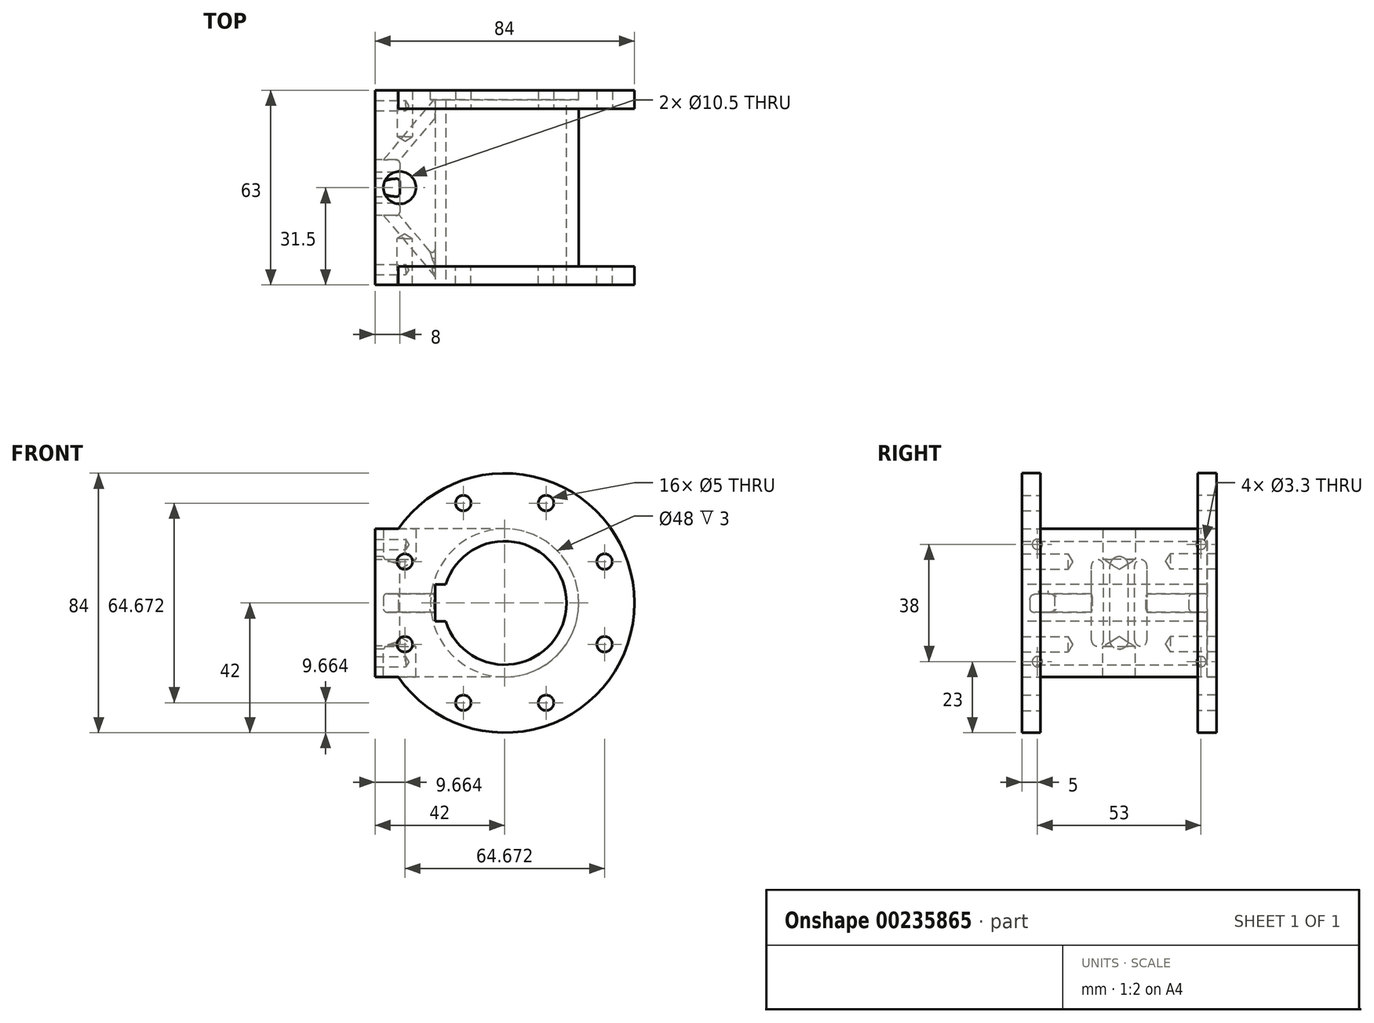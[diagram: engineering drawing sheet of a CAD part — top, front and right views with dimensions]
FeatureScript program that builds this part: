
annotation { "Feature Type Name" : "Feature", "Feature Type Description" : "" }
export const myFeature = defineFeature(function(context is Context, id is Id, definition is map)
    precondition{}
    {
        {
            var Q0;
            Q0=qCreatedBy(makeId("Front.planeOp"),FACE);
            var sketch = newSketch(context, id + "F0", { "sketchPlane" : qUnion([Q0])});
            skCircle(sketch, "E0", {"center": v(0, 0) * mm, "radius": 42 * mm});
            skCircle(sketch, "E1", {"center": v(0, 0) * mm, "radius": 35 * mm, "construction": true});
            skCircle(sketch, "E2", {"center": v(0, 0) * mm, "radius": 20 * mm});
            skCircle(sketch, "E3", {"center": v(-32.34, 13.4) * mm, "radius": 2.5 * mm});
            skCircle(sketch, "E4.1.0", {"center": v(-13.4, 32.34) * mm, "radius": 2.5 * mm});
            skCircle(sketch, "E4.2.0", {"center": v(13.4, 32.34) * mm, "radius": 2.5 * mm});
            skCircle(sketch, "E4.3.0", {"center": v(32.34, 13.4) * mm, "radius": 2.5 * mm});
            skCircle(sketch, "E4.4.0", {"center": v(32.34, -13.4) * mm, "radius": 2.5 * mm});
            skCircle(sketch, "E4.5.0", {"center": v(13.4, -32.34) * mm, "radius": 2.5 * mm});
            skCircle(sketch, "E4.6.0", {"center": v(-13.4, -32.34) * mm, "radius": 2.5 * mm});
            skCircle(sketch, "E4.7.0", {"center": v(-32.34, -13.4) * mm, "radius": 2.5 * mm});
            skLineSegment(sketch, "E4.anchor1", {"start": v(0, 0) * mm, "end": v(0, 35) * mm, "construction": true});
            skLineSegment(sketch, "E4.anchor2", {"start": v(0, 0) * mm, "end": v(-24.75, 24.75) * mm, "construction": true});
            skLineSegment(sketch, "E5", {"start": v(0, 0) * mm, "end": v(-54.86, 0) * mm, "construction": true});
            skLineSegment(sketch, "E6", {"start": v(-32.34, 13.4) * mm, "end": v(0, 0) * mm, "construction": true});
            skSolve(sketch);
        }
        {
            var Q0;
            Q0 = qSketchRegion(id + "F0", true);
            extrude(context, id + "F1", {"entities" : qUnion([Q0]), "depth" : 6 * mm});
        }
        {
            var Q0;
            Q0=qCreatedBy(makeId("Front.planeOp"),FACE);
            cPlane(context, id + "F2", {"entities" : qUnion([Q0]), "cplaneType" : CPlaneType.OFFSET, "offset" : 51 * mm, "oppositeDirection" : true, "width" : 150 * mm, "height" : 150 * mm});
        }
        {
            var Q0;
            Q0=qCreatedBy(id+"F2.planeOp",FACE);
            var sketch = newSketch(context, id + "F3", { "sketchPlane" : qUnion([Q0])});
            skCircle(sketch, "E7", {"center": v(0, 0) * mm, "radius": 42 * mm});
            skCircle(sketch, "E8", {"center": v(0, 0) * mm, "radius": 35 * mm, "construction": true});
            skCircle(sketch, "E9", {"center": v(0, 0) * mm, "radius": 20 * mm});
            skCircle(sketch, "E10", {"center": v(-32.34, 13.4) * mm, "radius": 2.5 * mm});
            skCircle(sketch, "E11.1.0", {"center": v(-32.34, -13.4) * mm, "radius": 2.5 * mm});
            skCircle(sketch, "E11.2.0", {"center": v(-13.4, -32.34) * mm, "radius": 2.5 * mm});
            skCircle(sketch, "E11.3.0", {"center": v(13.4, -32.34) * mm, "radius": 2.5 * mm});
            skCircle(sketch, "E11.4.0", {"center": v(32.34, -13.4) * mm, "radius": 2.5 * mm});
            skCircle(sketch, "E11.5.0", {"center": v(32.34, 13.4) * mm, "radius": 2.5 * mm});
            skCircle(sketch, "E11.6.0", {"center": v(13.4, 32.34) * mm, "radius": 2.5 * mm});
            skCircle(sketch, "E11.7.0", {"center": v(-13.4, 32.34) * mm, "radius": 2.5 * mm});
            skSolve(sketch);
        }
        {
            var Q0;
            Q0 = qSketchRegion(id + "F3", true);
            extrude(context, id + "F4", {"entities" : qUnion([Q0]), "oppositeDirection" : true, "depth" : 6 * mm});
        }
        {
            var Q0;
            Q0=qCreatedBy(makeId("Front.planeOp"),FACE);
            var sketch = newSketch(context, id + "F5", { "sketchPlane" : qUnion([Q0])});
            skCircle(sketch, "E12", {"center": v(0, 0) * mm, "radius": 24 * mm});
            skLineSegment(sketch, "E13", {"start": v(0, 24) * mm, "end": v(-42, 24) * mm});
            skLineSegment(sketch, "E14.0", {"start": v(0, -24) * mm, "end": v(-42, -24) * mm});
            skLineSegment(sketch, "E15", {"start": v(-42, 24) * mm, "end": v(-42, -24) * mm});
            skArc(sketch, "E16", {"start": v(-19.08, -6) * mm, "mid": v(20, 0) * mm, "end": v(-19.08, 6) * mm});
            skLineSegment(sketch, "E17", {"start": v(-22.52, -6) * mm, "end": v(-22.52, 6) * mm});
            skLineSegment(sketch, "E18", {"start": v(-22.52, 6) * mm, "end": v(-19.08, 6) * mm});
            skLineSegment(sketch, "E19", {"start": v(-19.08, -6) * mm, "end": v(-22.52, -6) * mm});
            skSolve(sketch);
        }
        {
            var Q0;
            {var subQ0=sQuery(id+"F5.wireOp",EDGE,"E13");Q0=makeQuery(id+"F5.imprint","IMPRINT",FACE,{"disambiguationData":[TD([[makeQuery(id+"F5.imprint","IMPRINT",EDGE,{"derivedFrom":subQ0}),1.0]])]});}
            var Q1;
            Q1=makeQuery(id+"F5.imprint","IMPRINT",FACE,{"disambiguationData":[TD([[makeQuery(id+"F5.imprint","IMPRINT",EDGE,{"derivedFrom":sQuery(id+"F5.wireOp",EDGE,"E16")}),-1.0]])]});
            var Q2;
            Q2=makeQuery(id+"F4.opExtrude","CAP_FACE",FACE,{"disambiguationData":[OSD([sQuery(id+"F3.wireOp",EDGE,"E7"),sQuery(id+"F3.wireOp",EDGE,"E9"),sQuery(id+"F3.wireOp",EDGE,"E10"),sQuery(id+"F3.wireOp",EDGE,"E11.1.0"),sQuery(id+"F3.wireOp",EDGE,"E11.2.0"),sQuery(id+"F3.wireOp",EDGE,"E11.3.0"),sQuery(id+"F3.wireOp",EDGE,"E11.4.0"),sQuery(id+"F3.wireOp",EDGE,"E11.5.0"),sQuery(id+"F3.wireOp",EDGE,"E11.6.0"),sQuery(id+"F3.wireOp",EDGE,"E11.7.0")])],"isStart":false});
            extrude(context, id + "F6", {"entities" : qUnion([Q0, Q1]), "operationType" : NewBodyOperationType.ADD, "endBound" : BoundingType.UP_TO_SURFACE, "oppositeDirection" : true, "endBoundEntityFace" : qUnion([Q2]), "depth" : 25 * mm});
        }
        {
            var Q0;
            {var subQ0=sQuery(id+"F5.wireOp",EDGE,"E13");Q0=makeQuery(id+"F5.imprint","IMPRINT",FACE,{"disambiguationData":[TD([[makeQuery(id+"F5.imprint","IMPRINT",EDGE,{"derivedFrom":subQ0}),1.0]])]});}
            var Q1;
            Q1=makeQuery(id+"F5.imprint","IMPRINT",FACE,{"disambiguationData":[TD([[makeQuery(id+"F5.imprint","IMPRINT",EDGE,{"derivedFrom":sQuery(id+"F5.wireOp",EDGE,"E16")}),-1.0]])]});
            extrude(context, id + "F7", {"entities" : qUnion([Q0, Q1]), "operationType" : NewBodyOperationType.ADD, "depth" : 6 * mm});
        }
        {
            var Q0;
            Q0=makeQuery(id+"F5.imprint","IMPRINT",FACE,{"disambiguationData":[TD([[makeQuery(id+"F5.imprint","IMPRINT",EDGE,{"derivedFrom":sQuery(id+"F5.wireOp",EDGE,"E16")}),1.0]])]});
            extrude(context, id + "F8", {"entities" : qUnion([Q0]), "operationType" : NewBodyOperationType.REMOVE, "oppositeDirection" : true, "depth" : 222 * mm, "symmetric" : true});
        }
        {
            var Q0;
            Q0=qCreatedBy(makeId("Front.planeOp"),FACE);
            cPlane(context, id + "F9", {"entities" : qUnion([Q0]), "cplaneType" : CPlaneType.OFFSET, "offset" : 6 * mm, "width" : 150 * mm, "height" : 150 * mm});
        }
        {
            var Q0;
            Q0=qCreatedBy(id+"F9.planeOp",FACE);
            var sketch = newSketch(context, id + "F10", { "sketchPlane" : qUnion([Q0])});
            skCircle(sketch, "E20", {"center": v(0, 0) * mm, "radius": 35 * mm, "construction": true});
            skCircle(sketch, "E21", {"center": v(-32.34, 13.4) * mm, "radius": 2.5 * mm});
            skCircle(sketch, "E22.1.0", {"center": v(-32.34, -13.4) * mm, "radius": 2.5 * mm});
            skCircle(sketch, "E22.2.0", {"center": v(-13.4, -32.34) * mm, "radius": 2.5 * mm});
            skCircle(sketch, "E22.3.0", {"center": v(13.4, -32.34) * mm, "radius": 2.5 * mm});
            skCircle(sketch, "E22.4.0", {"center": v(32.34, -13.4) * mm, "radius": 2.5 * mm});
            skCircle(sketch, "E22.5.0", {"center": v(32.34, 13.4) * mm, "radius": 2.5 * mm});
            skCircle(sketch, "E22.6.0", {"center": v(13.4, 32.34) * mm, "radius": 2.5 * mm});
            skCircle(sketch, "E22.7.0", {"center": v(-13.4, 32.34) * mm, "radius": 2.5 * mm});
            skSolve(sketch);
        }
        {
            var Q0;
            Q0=sQuery(id+"F10.wireOp",VERTEX,"E21.center");
            var Q1;
            Q1=sQuery(id+"F10.wireOp",VERTEX,"E22.1.0.center");
            var Q2;
            Q2=sQuery(id+"F10.wireOp",VERTEX,"E22.7.0.center");
            var Q3;
            Q3=sQuery(id+"F10.wireOp",VERTEX,"E22.6.0.center");
            var Q4;
            Q4=sQuery(id+"F10.wireOp",VERTEX,"E22.5.0.center");
            var Q5;
            Q5=sQuery(id+"F10.wireOp",VERTEX,"E22.4.0.center");
            var Q6;
            Q6=sQuery(id+"F10.wireOp",VERTEX,"E22.3.0.center");
            var Q7;
            Q7=sQuery(id+"F10.wireOp",VERTEX,"E22.2.0.center");
            var Q8;
            Q8=makeQuery(id+"F1.opExtrude","SWEPT_BODY",BODY,{"disambiguationData":[OSD([sQuery(id+"F0.wireOp",EDGE,"E0"),sQuery(id+"F0.wireOp",EDGE,"E2"),sQuery(id+"F0.wireOp",EDGE,"E3"),sQuery(id+"F0.wireOp",EDGE,"E4.1.0"),sQuery(id+"F0.wireOp",EDGE,"E4.2.0"),sQuery(id+"F0.wireOp",EDGE,"E4.3.0"),sQuery(id+"F0.wireOp",EDGE,"E4.4.0"),sQuery(id+"F0.wireOp",EDGE,"E4.5.0"),sQuery(id+"F0.wireOp",EDGE,"E4.6.0"),sQuery(id+"F0.wireOp",EDGE,"E4.7.0")])]});
            hole(context, id + "F11", {"style" : HoleStyle.SIMPLE, "endStyle" : HoleEndStyle.BLIND, "standardTappedOrClearance" : lookupTablePath({ "standard" : "ISO", "engagement" : "75%", "pitch" : "1 mm", "size" : "M6", "type" : "Tapped" }), "standardBlindInLast" : lookupTablePath({ "standard" : "ISO", "engagement" : "75%", "pitch" : "1 mm", "size" : "M6", "type" : "Tapped" }), "holeDiameter" : 5 * mm, "showTappedDepth" : true, "holeDepth" : 15 * mm, "tappedDepth" : 12 * mm, "tapClearance" : 3, "startFromSketch" : true, "locations" : qUnion([Q0, Q1, Q2, Q3, Q4, Q5, Q6, Q7]), "scope" : qUnion([Q8]), "majorDiameter" : 6 * mm});
        }
        {
            var Q0;
            Q0=qCreatedBy(id+"F2.planeOp",FACE);
            cPlane(context, id + "F12", {"entities" : qUnion([Q0]), "cplaneType" : CPlaneType.OFFSET, "offset" : 6 * mm, "oppositeDirection" : true, "width" : 150 * mm, "height" : 150 * mm});
        }
        {
            var Q0;
            Q0=qCreatedBy(id+"F12.planeOp",FACE);
            var sketch = newSketch(context, id + "F13", { "sketchPlane" : qUnion([Q0])});
            skCircle(sketch, "E23", {"center": v(0, 0) * mm, "radius": 35 * mm});
            skCircle(sketch, "E24", {"center": v(-32.34, 13.4) * mm, "radius": 2.5 * mm});
            skCircle(sketch, "E25.1.0", {"center": v(-32.34, -13.4) * mm, "radius": 2.5 * mm});
            skCircle(sketch, "E25.2.0", {"center": v(-13.4, -32.34) * mm, "radius": 2.5 * mm});
            skCircle(sketch, "E25.3.0", {"center": v(13.4, -32.34) * mm, "radius": 2.5 * mm});
            skCircle(sketch, "E25.4.0", {"center": v(32.34, -13.4) * mm, "radius": 2.5 * mm});
            skCircle(sketch, "E25.5.0", {"center": v(32.34, 13.4) * mm, "radius": 2.5 * mm});
            skCircle(sketch, "E25.6.0", {"center": v(13.4, 32.34) * mm, "radius": 2.5 * mm});
            skCircle(sketch, "E25.7.0", {"center": v(-13.4, 32.34) * mm, "radius": 2.5 * mm});
            skSolve(sketch);
        }
        {
            var Q0;
            Q0=sQuery(id+"F13.wireOp",VERTEX,"E25.6.0.center");
            var Q1;
            Q1=sQuery(id+"F13.wireOp",VERTEX,"E25.5.0.center");
            var Q2;
            Q2=sQuery(id+"F13.wireOp",VERTEX,"E25.4.0.center");
            var Q3;
            Q3=sQuery(id+"F13.wireOp",VERTEX,"E25.3.0.center");
            var Q4;
            Q4=sQuery(id+"F13.wireOp",VERTEX,"E25.2.0.center");
            var Q5;
            Q5=sQuery(id+"F13.wireOp",VERTEX,"E25.1.0.center");
            var Q6;
            Q6=sQuery(id+"F13.wireOp",VERTEX,"E24.center");
            var Q7;
            Q7=sQuery(id+"F13.wireOp",VERTEX,"E25.7.0.center");
            var Q8;
            Q8=makeQuery(id+"F1.opExtrude","SWEPT_BODY",BODY,{"disambiguationData":[OSD([sQuery(id+"F0.wireOp",EDGE,"E0"),sQuery(id+"F0.wireOp",EDGE,"E2"),sQuery(id+"F0.wireOp",EDGE,"E3"),sQuery(id+"F0.wireOp",EDGE,"E4.1.0"),sQuery(id+"F0.wireOp",EDGE,"E4.2.0"),sQuery(id+"F0.wireOp",EDGE,"E4.3.0"),sQuery(id+"F0.wireOp",EDGE,"E4.4.0"),sQuery(id+"F0.wireOp",EDGE,"E4.5.0"),sQuery(id+"F0.wireOp",EDGE,"E4.6.0"),sQuery(id+"F0.wireOp",EDGE,"E4.7.0")])]});
            hole(context, id + "F14", {"style" : HoleStyle.SIMPLE, "endStyle" : HoleEndStyle.BLIND, "oppositeDirection" : true, "standardTappedOrClearance" : lookupTablePath({ "standard" : "ISO", "engagement" : "75%", "pitch" : "1 mm", "size" : "M6", "type" : "Tapped" }), "standardBlindInLast" : lookupTablePath({ "standard" : "ISO", "engagement" : "75%", "pitch" : "1 mm", "size" : "M6", "type" : "Tapped" }), "holeDiameter" : 5 * mm, "showTappedDepth" : true, "holeDepth" : 15 * mm, "tappedDepth" : 12 * mm, "tapClearance" : 3, "startFromSketch" : true, "locations" : qUnion([Q0, Q1, Q2, Q3, Q4, Q5, Q6, Q7]), "scope" : qUnion([Q8]), "majorDiameter" : 6 * mm});
        }
        {
            var Q0;
            Q0=qCreatedBy(makeId("Top.planeOp"),FACE);
            cPlane(context, id + "F15", {"entities" : qUnion([Q0]), "cplaneType" : CPlaneType.OFFSET, "offset" : 24 * mm, "oppositeDirection" : true, "width" : 150 * mm, "height" : 150 * mm});
        }
        {
            var Q0;
            Q0=qCreatedBy(id+"F15.planeOp",FACE);
            var sketch = newSketch(context, id + "F16", { "sketchPlane" : qUnion([Q0])});
            skLineSegment(sketch, "E26", {"start": v(0, 0) * mm, "end": v(0, 25.5) * mm});
            skLineSegment(sketch, "E27", {"start": v(0, 25.5) * mm, "end": v(-42, 25.5) * mm});
            skLineSegment(sketch, "E28", {"start": v(-42, 25.5) * mm, "end": v(-34, 25.5) * mm});
            skSolve(sketch);
        }
        {
            var Q0;
            Q0=sQuery(id+"F16.wireOp",VERTEX,"E28.end");
            var Q1;
            Q1=makeQuery(id+"F1.opExtrude","SWEPT_BODY",BODY,{"disambiguationData":[OSD([sQuery(id+"F0.wireOp",EDGE,"E0"),sQuery(id+"F0.wireOp",EDGE,"E2"),sQuery(id+"F0.wireOp",EDGE,"E3"),sQuery(id+"F0.wireOp",EDGE,"E4.1.0"),sQuery(id+"F0.wireOp",EDGE,"E4.2.0"),sQuery(id+"F0.wireOp",EDGE,"E4.3.0"),sQuery(id+"F0.wireOp",EDGE,"E4.4.0"),sQuery(id+"F0.wireOp",EDGE,"E4.5.0"),sQuery(id+"F0.wireOp",EDGE,"E4.6.0"),sQuery(id+"F0.wireOp",EDGE,"E4.7.0")])]});
            hole(context, id + "F17", {"style" : HoleStyle.SIMPLE, "endStyle" : HoleEndStyle.BLIND, "oppositeDirection" : true, "standardTappedOrClearance" : lookupTablePath({ "standard" : "ISO", "engagement" : "75%", "pitch" : "1.5 mm", "size" : "M12", "type" : "Tapped" }), "standardBlindInLast" : lookupTablePath({ "standard" : "ISO", "engagement" : "75%", "pitch" : "1.5 mm", "size" : "M12", "type" : "Tapped" }), "holeDiameter" : 10.5 * mm, "showTappedDepth" : true, "holeDepth" : 9.9 * mm, "tappedDepth" : 7.87 * mm, "tapClearance" : 10, "startFromSketch" : true, "locations" : qUnion([Q0]), "scope" : qUnion([Q1]), "majorDiameter" : 12 * mm});
        }
        {
            var Q0;
            Q0=qCreatedBy(makeId("Right.planeOp"),FACE);
            cPlane(context, id + "F18", {"entities" : qUnion([Q0]), "cplaneType" : CPlaneType.OFFSET, "offset" : 42 * mm, "oppositeDirection" : true, "width" : 150 * mm, "height" : 150 * mm});
        }
        {
            var Q0;
            Q0=qCreatedBy(id+"F18.planeOp",FACE);
            var sketch = newSketch(context, id + "F19", { "sketchPlane" : qUnion([Q0])});
            skLineSegment(sketch, "E29", {"start": v(0, 0) * mm, "end": v(84.51, 0) * mm, "construction": true});
            skLineSegment(sketch, "E30", {"start": v(0, 0) * mm, "end": v(-48.74, 0) * mm, "construction": true});
            skLineSegment(sketch, "E31.0", {"start": v(0, 19) * mm, "end": v(-48.74, 19) * mm, "construction": true});
            skLineSegment(sketch, "E31.1", {"start": v(0, 19) * mm, "end": v(84.51, 19) * mm, "construction": true});
            skLineSegment(sketch, "E32.0", {"start": v(0, -19) * mm, "end": v(-48.74, -19) * mm, "construction": true});
            skLineSegment(sketch, "E32.1", {"start": v(0, -19) * mm, "end": v(84.51, -19) * mm, "construction": true});
            skLineSegment(sketch, "E33.0", {"start": v(25.5, 0) * mm, "end": v(25.5, -48.56) * mm, "construction": true});
            skLineSegment(sketch, "E33.1", {"start": v(25.5, 0) * mm, "end": v(25.5, 55.03) * mm, "construction": true});
            skLineSegment(sketch, "E34.0", {"start": v(52, 0) * mm, "end": v(52, 55.03) * mm, "construction": true});
            skLineSegment(sketch, "E34.1", {"start": v(52, 0) * mm, "end": v(52, -48.56) * mm, "construction": true});
            skLineSegment(sketch, "E35.0", {"start": v(-1, 0) * mm, "end": v(-1, 55.03) * mm, "construction": true});
            skLineSegment(sketch, "E35.1", {"start": v(-1, 0) * mm, "end": v(-1, -48.56) * mm, "construction": true});
            skCircle(sketch, "E36", {"center": v(52, 19) * mm, "radius": 1.65 * mm});
            skCircle(sketch, "E37.MirrorC", {"center": v(-1, 19) * mm, "radius": 1.65 * mm});
            skCircle(sketch, "E38.MirrorC", {"center": v(-1, -19) * mm, "radius": 1.65 * mm});
            skCircle(sketch, "E39.MirrorC", {"center": v(52, -19) * mm, "radius": 1.65 * mm});
            skLineSegment(sketch, "E40.0", {"start": v(0, 6) * mm, "end": v(84.51, 6) * mm, "construction": true});
            skLineSegment(sketch, "E40.1", {"start": v(0, 6) * mm, "end": v(-48.74, 6) * mm, "construction": true});
            skLineSegment(sketch, "E41.0", {"start": v(0, -6) * mm, "end": v(84.51, -6) * mm, "construction": true});
            skLineSegment(sketch, "E41.1", {"start": v(0, -6) * mm, "end": v(-48.74, -6) * mm, "construction": true});
            skLineSegment(sketch, "E42.0", {"start": v(0, 12) * mm, "end": v(-48.74, 12) * mm, "construction": true});
            skLineSegment(sketch, "E42.1", {"start": v(0, 12) * mm, "end": v(84.51, 12) * mm, "construction": true});
            skLineSegment(sketch, "E43.0", {"start": v(0, -12) * mm, "end": v(-48.74, -12) * mm, "construction": true});
            skLineSegment(sketch, "E43.1", {"start": v(0, -12) * mm, "end": v(84.51, -12) * mm, "construction": true});
            skLineSegment(sketch, "E44.0", {"start": v(32.5, 0) * mm, "end": v(32.5, 55.03) * mm, "construction": true});
            skLineSegment(sketch, "E44.1", {"start": v(32.5, 0) * mm, "end": v(32.5, -48.56) * mm, "construction": true});
            skLineSegment(sketch, "E45.0", {"start": v(18.5, 0) * mm, "end": v(18.5, 55.03) * mm, "construction": true});
            skLineSegment(sketch, "E45.1", {"start": v(18.5, 0) * mm, "end": v(18.5, -48.56) * mm, "construction": true});
            skArc(sketch, "E46", {"start": v(34.5, 12) * mm, "mid": v(32.5, 14) * mm, "end": v(30.5, 12) * mm});
            skArc(sketch, "E47", {"start": v(28.5, 12) * mm, "mid": v(25.5, 15) * mm, "end": v(22.5, 12) * mm});
            skArc(sketch, "E48.MirrorC", {"start": v(34.5, -12) * mm, "mid": v(32.5, -14) * mm, "end": v(30.5, -12) * mm});
            skArc(sketch, "E49.MirrorC", {"start": v(16.5, 12) * mm, "mid": v(18.5, 14) * mm, "end": v(20.5, 12) * mm});
            skArc(sketch, "E50.MirrorC", {"start": v(16.5, -12) * mm, "mid": v(18.5, -14) * mm, "end": v(20.5, -12) * mm});
            skArc(sketch, "E51.MirrorC", {"start": v(28.5, -12) * mm, "mid": v(25.5, -15) * mm, "end": v(22.5, -12) * mm});
            skLineSegment(sketch, "E52", {"start": v(34.5, -12) * mm, "end": v(34.5, 12) * mm});
            skLineSegment(sketch, "E53", {"start": v(30.5, -12) * mm, "end": v(30.5, 12) * mm});
            skLineSegment(sketch, "E54", {"start": v(28.5, -12) * mm, "end": v(28.5, 12) * mm});
            skLineSegment(sketch, "E55", {"start": v(22.5, -12) * mm, "end": v(22.5, 12) * mm});
            skLineSegment(sketch, "E56.MirrorCS", {"start": v(16.5, -12) * mm, "end": v(16.5, 12) * mm});
            skLineSegment(sketch, "E57.MirrorCS", {"start": v(20.5, -12) * mm, "end": v(20.5, 12) * mm});
            skSolve(sketch);
        }
        {
            var Q0;
            Q0=sQuery(id+"F19.wireOp",VERTEX,"E36.center");
            var Q1;
            Q1=sQuery(id+"F19.wireOp",VERTEX,"E37.MirrorC.center");
            var Q2;
            Q2=sQuery(id+"F19.wireOp",VERTEX,"E38.MirrorC.center");
            var Q3;
            Q3=sQuery(id+"F19.wireOp",VERTEX,"E39.MirrorC.center");
            var Q4;
            Q4=makeQuery(id+"F1.opExtrude","SWEPT_BODY",BODY,{"disambiguationData":[OSD([sQuery(id+"F0.wireOp",EDGE,"E0"),sQuery(id+"F0.wireOp",EDGE,"E2"),sQuery(id+"F0.wireOp",EDGE,"E3"),sQuery(id+"F0.wireOp",EDGE,"E4.1.0"),sQuery(id+"F0.wireOp",EDGE,"E4.2.0"),sQuery(id+"F0.wireOp",EDGE,"E4.3.0"),sQuery(id+"F0.wireOp",EDGE,"E4.4.0"),sQuery(id+"F0.wireOp",EDGE,"E4.5.0"),sQuery(id+"F0.wireOp",EDGE,"E4.6.0"),sQuery(id+"F0.wireOp",EDGE,"E4.7.0")])]});
            hole(context, id + "F20", {"style" : HoleStyle.SIMPLE, "endStyle" : HoleEndStyle.BLIND, "oppositeDirection" : true, "standardTappedOrClearance" : lookupTablePath({ "standard" : "ISO", "engagement" : "75%", "pitch" : "0.7 mm", "size" : "M4", "type" : "Tapped" }), "standardBlindInLast" : lookupTablePath({ "standard" : "ISO", "engagement" : "75%", "pitch" : "0.7 mm", "size" : "M4", "type" : "Tapped" }), "holeDiameter" : 3.3 * mm, "showTappedDepth" : true, "holeDepth" : 10 * mm, "tappedDepth" : 7.9 * mm, "tapClearance" : 3, "startFromSketch" : true, "locations" : qUnion([Q0, Q1, Q2, Q3]), "scope" : qUnion([Q4]), "majorDiameter" : 4 * mm});
        }
        {
            var Q0;
            Q0 = qSketchRegion(id + "F19", true);
            extrude(context, id + "F21", {"entities" : qUnion([Q0]), "operationType" : NewBodyOperationType.REMOVE, "depth" : 8 * mm});
        }
        {
            var Q0;
            Q0=makeQuery(id+"F21.boolean.opBoolean","COPY",FACE,{"derivedFrom":makeQuery(id+"F21.opExtrude","CAP_FACE",FACE,{"disambiguationData":[OSD([sQuery(id+"F19.wireOp",EDGE,"E49.MirrorC"),sQuery(id+"F19.wireOp",EDGE,"E50.MirrorC"),sQuery(id+"F19.wireOp",EDGE,"E56.MirrorCS"),sQuery(id+"F19.wireOp",EDGE,"E57.MirrorCS")])],"isStart":false})});
            var Q1;
            Q1=makeQuery(id+"F21.boolean.opBoolean","COPY",FACE,{"derivedFrom":makeQuery(id+"F21.opExtrude","CAP_FACE",FACE,{"disambiguationData":[OSD([sQuery(id+"F19.wireOp",EDGE,"E46"),sQuery(id+"F19.wireOp",EDGE,"E48.MirrorC"),sQuery(id+"F19.wireOp",EDGE,"E52"),sQuery(id+"F19.wireOp",EDGE,"E53")])],"isStart":false})});
            var Q2;
            Q2=makeQuery(id+"F21.boolean.opBoolean","COPY",EDGE,{"derivedFrom":makeQuery(id+"F21.opExtrude","CAP_EDGE",EDGE,{"disambiguationData":[OSD([sQuery(id+"F19.wireOp",EDGE,"E55")])],"isStart":false})});
            fillet(context, id + "F22", {"entities" : qUnion([Q0, Q1, Q2]), "radius" : 1 * mm, "tangentPropagation" : true, "allowEdgeOverflow" : false});
        }
        {
            var Q0;
            Q0=qCreatedBy(id+"F12.planeOp",FACE);
            var sketch = newSketch(context, id + "F23", { "sketchPlane" : qUnion([Q0])});
            skCircle(sketch, "E58", {"center": v(0, 0) * mm, "radius": 24 * mm});
            skSolve(sketch);
        }
        {
            var Q0;
            Q0=makeQuery(id+"F23.imprint","IMPRINT",FACE,{"disambiguationData":[TD([[makeQuery(id+"F23.imprint","IMPRINT",EDGE,{"derivedFrom":sQuery(id+"F23.wireOp",EDGE,"E58")}),1.0]])]});
            extrude(context, id + "F24", {"entities" : qUnion([Q0]), "operationType" : NewBodyOperationType.REMOVE, "depth" : 3 * mm});
        }
        {
            var Q0;
            Q0=qCreatedBy(makeId("Top.planeOp"),FACE);
            var sketch = newSketch(context, id + "F25", { "sketchPlane" : qUnion([Q0])});
            skLineSegment(sketch, "E59", {"start": v(0, 0) * mm, "end": v(0, 25.5) * mm, "construction": true});
            skLineSegment(sketch, "E60", {"start": v(0, 25.5) * mm, "end": v(-42, 25.5) * mm, "construction": true});
            skLineSegment(sketch, "E61", {"start": v(-42, 25.5) * mm, "end": v(-34, 25.5) * mm});
            skLineSegment(sketch, "E62", {"start": v(-34, 25.5) * mm, "end": v(-34, 16.5) * mm, "construction": true});
            skLineSegment(sketch, "E63", {"start": v(-34, 16.5) * mm, "end": v(-42, 16.5) * mm, "construction": true});
            skLineSegment(sketch, "E64.MirrorCS", {"start": v(-34, 25.5) * mm, "end": v(-34, 34.5) * mm});
            skLineSegment(sketch, "E65.MirrorCS", {"start": v(-34, 34.5) * mm, "end": v(-42, 34.5) * mm});
            skLineSegment(sketch, "E66", {"start": v(-42, 16.5) * mm, "end": v(-42, 0) * mm, "construction": true});
            skLineSegment(sketch, "E67", {"start": v(-42, 0) * mm, "end": v(0, 0) * mm, "construction": true});
            skLineSegment(sketch, "E68", {"start": v(-34, 16.5) * mm, "end": v(-36, 16.5) * mm});
            skPoint(sketch, "E69", {"position": v(-21, 0) * mm});
            skLineSegment(sketch, "E70", {"start": v(-34, 16.5) * mm, "end": v(-34.57, 17.18) * mm});
            skLineSegment(sketch, "E71", {"start": v(-34, 16.5) * mm, "end": v(-21.65, 1.81) * mm});
            skLineSegment(sketch, "E72.0", {"start": v(-39.8, 17.18) * mm, "end": v(-27.13, 2.12) * mm});
            skLineSegment(sketch, "E73", {"start": v(-34.57, 17.18) * mm, "end": v(-39.8, 17.18) * mm});
            skLineSegment(sketch, "E74", {"start": v(-21.65, 1.81) * mm, "end": v(-21.65, -4.4) * mm});
            skLineSegment(sketch, "E75", {"start": v(-27.13, 2.12) * mm, "end": v(-21.65, -4.4) * mm});
            skLineSegment(sketch, "E76.MirrorCS", {"start": v(-34.57, 33.82) * mm, "end": v(-39.8, 33.82) * mm});
            skLineSegment(sketch, "E77.MirrorCS", {"start": v(-34, 34.5) * mm, "end": v(-21.65, 49.19) * mm});
            skLineSegment(sketch, "E78.MirrorCS", {"start": v(-39.8, 33.82) * mm, "end": v(-27.13, 48.88) * mm});
            skLineSegment(sketch, "E79.MirrorCS", {"start": v(-27.13, 48.88) * mm, "end": v(-21.65, 55.4) * mm});
            skLineSegment(sketch, "E80.MirrorCS", {"start": v(-21.65, 49.19) * mm, "end": v(-21.65, 55.4) * mm});
            skLineSegment(sketch, "E81.MirrorCS", {"start": v(-34, 34.5) * mm, "end": v(-34.57, 33.82) * mm});
            skSolve(sketch);
        }
        {
            var Q0;
            Q0 = qSketchRegion(id + "F25", true);
            extrude(context, id + "F26", {"entities" : qUnion([Q0]), "operationType" : NewBodyOperationType.REMOVE, "oppositeDirection" : true, "depth" : 6 * mm, "symmetric" : true});
        }
        {
            var Q0;
            Q0=makeQuery(id+"F26.boolean.opBoolean","COPY",EDGE,{"derivedFrom":makeQuery(id+"F26.opExtrude","CAP_EDGE",EDGE,{"disambiguationData":[OSD([sQuery(id+"F25.wireOp",EDGE,"E70"),sQuery(id+"F25.wireOp",EDGE,"E71")])],"isStart":false})});
            var Q1;
            Q1=makeQuery(id+"F26.boolean.opBoolean","COPY",EDGE,{"derivedFrom":makeQuery(id+"F26.opExtrude","CAP_EDGE",EDGE,{"disambiguationData":[OSD([sQuery(id+"F25.wireOp",EDGE,"E70"),sQuery(id+"F25.wireOp",EDGE,"E71")])],"isStart":true})});
            var Q2;
            {var subQ0=sQuery(id+"F5.wireOp",EDGE,"E17");Q2=makeQuery(id+"F26.boolean.opBoolean","INTERSECT",EDGE,{"derivedFrom":[makeQuery(id+"F8.boolean.opBoolean","MERGE",FACE,{"derivedFrom":[makeQuery(id+"F6.opExtrude","SWEPT_FACE",FACE,{"disambiguationData":[OSD([subQ0])]}),makeQuery(id+"F8.opExtrude","SWEPT_FACE",FACE,{"disambiguationData":[OSD([subQ0])]})]}),makeQuery(id+"F26.opExtrude","SWEPT_FACE",FACE,{"disambiguationData":[OSD([sQuery(id+"F25.wireOp",EDGE,"E70"),sQuery(id+"F25.wireOp",EDGE,"E71")])]})]});}
            var Q3;
            Q3=makeQuery(id+"F26.boolean.opBoolean","COPY",EDGE,{"derivedFrom":makeQuery(id+"F26.opExtrude","CAP_EDGE",EDGE,{"disambiguationData":[OSD([sQuery(id+"F25.wireOp",EDGE,"E77.MirrorCS"),sQuery(id+"F25.wireOp",EDGE,"E81.MirrorCS")])],"isStart":false})});
            var Q4;
            Q4=makeQuery(id+"F26.boolean.opBoolean","COPY",EDGE,{"derivedFrom":makeQuery(id+"F26.opExtrude","CAP_EDGE",EDGE,{"disambiguationData":[OSD([sQuery(id+"F25.wireOp",EDGE,"E77.MirrorCS"),sQuery(id+"F25.wireOp",EDGE,"E81.MirrorCS")])],"isStart":true})});
            var Q5;
            Q5=makeQuery(id+"F26.boolean.opBoolean","COPY",EDGE,{"derivedFrom":makeQuery(id+"F26.opExtrude","CAP_EDGE",EDGE,{"disambiguationData":[OSD([sQuery(id+"F25.wireOp",EDGE,"E72.0"),sQuery(id+"F25.wireOp",EDGE,"E75")])],"isStart":true})});
            var Q6;
            Q6=makeQuery(id+"F26.boolean.opBoolean","COPY",EDGE,{"derivedFrom":makeQuery(id+"F26.opExtrude","CAP_EDGE",EDGE,{"disambiguationData":[OSD([sQuery(id+"F25.wireOp",EDGE,"E72.0"),sQuery(id+"F25.wireOp",EDGE,"E75")])],"isStart":false})});
            var Q7;
            Q7=makeQuery(id+"F26.boolean.opBoolean","COPY",EDGE,{"derivedFrom":makeQuery(id+"F26.opExtrude","CAP_EDGE",EDGE,{"disambiguationData":[OSD([sQuery(id+"F25.wireOp",EDGE,"E78.MirrorCS"),sQuery(id+"F25.wireOp",EDGE,"E79.MirrorCS")])],"isStart":false})});
            var Q8;
            Q8=makeQuery(id+"F26.boolean.opBoolean","COPY",EDGE,{"derivedFrom":makeQuery(id+"F26.opExtrude","CAP_EDGE",EDGE,{"disambiguationData":[OSD([sQuery(id+"F25.wireOp",EDGE,"E78.MirrorCS"),sQuery(id+"F25.wireOp",EDGE,"E79.MirrorCS")])],"isStart":true})});
            var Q9;
            {var subQ0=sQuery(id+"F5.wireOp",EDGE,"E17");Q9=makeQuery(id+"F26.boolean.opBoolean","INTERSECT",EDGE,{"derivedFrom":[makeQuery(id+"F8.boolean.opBoolean","MERGE",FACE,{"derivedFrom":[makeQuery(id+"F6.opExtrude","SWEPT_FACE",FACE,{"disambiguationData":[OSD([subQ0])]}),makeQuery(id+"F8.opExtrude","SWEPT_FACE",FACE,{"disambiguationData":[OSD([subQ0])]})]}),makeQuery(id+"F26.opExtrude","CAP_FACE",FACE,{"disambiguationData":[OSD([sQuery(id+"F25.wireOp",EDGE,"E70"),sQuery(id+"F25.wireOp",EDGE,"E71"),sQuery(id+"F25.wireOp",EDGE,"E72.0"),sQuery(id+"F25.wireOp",EDGE,"E73"),sQuery(id+"F25.wireOp",EDGE,"E74"),sQuery(id+"F25.wireOp",EDGE,"E75")])],"isStart":true})]});}
            fillet(context, id + "F27", {"entities" : qUnion([Q0, Q1, Q2, Q3, Q4, Q5, Q6, Q7, Q8, Q9]), "radius" : 1 * mm, "tangentPropagation" : true, "allowEdgeOverflow" : false});
        }
        {
            var Q0;
            Q0=qCreatedBy(makeId("Top.planeOp"),FACE);
            cPlane(context, id + "F28", {"entities" : qUnion([Q0]), "cplaneType" : CPlaneType.OFFSET, "offset" : 24 * mm, "width" : 150 * mm, "height" : 150 * mm});
        }
        {
            var Q0;
            Q0=qCreatedBy(id+"F28.planeOp",FACE);
            var sketch = newSketch(context, id + "F29", { "sketchPlane" : qUnion([Q0])});
            skLineSegment(sketch, "E82", {"start": v(0, 0) * mm, "end": v(0, 25.5) * mm});
            skLineSegment(sketch, "E83", {"start": v(0, 25.5) * mm, "end": v(-34, 25.5) * mm});
            skSolve(sketch);
        }
        {
            var Q0;
            Q0=sQuery(id+"F29.wireOp",VERTEX,"E83.end");
            var Q1;
            Q1=makeQuery(id+"F1.opExtrude","SWEPT_BODY",BODY,{"disambiguationData":[OSD([sQuery(id+"F0.wireOp",EDGE,"E0"),sQuery(id+"F0.wireOp",EDGE,"E2"),sQuery(id+"F0.wireOp",EDGE,"E3"),sQuery(id+"F0.wireOp",EDGE,"E4.1.0"),sQuery(id+"F0.wireOp",EDGE,"E4.2.0"),sQuery(id+"F0.wireOp",EDGE,"E4.3.0"),sQuery(id+"F0.wireOp",EDGE,"E4.4.0"),sQuery(id+"F0.wireOp",EDGE,"E4.5.0"),sQuery(id+"F0.wireOp",EDGE,"E4.6.0"),sQuery(id+"F0.wireOp",EDGE,"E4.7.0")])]});
            hole(context, id + "F30", {"style" : HoleStyle.SIMPLE, "endStyle" : HoleEndStyle.BLIND, "standardTappedOrClearance" : lookupTablePath({ "standard" : "ISO", "engagement" : "75%", "pitch" : "1.5 mm", "size" : "M12", "type" : "Tapped" }), "standardBlindInLast" : lookupTablePath({ "standard" : "ISO", "engagement" : "75%", "pitch" : "1.5 mm", "size" : "M12", "type" : "Tapped" }), "holeDiameter" : 10.5 * mm, "showTappedDepth" : true, "holeDepth" : 9.9 * mm, "tappedDepth" : 7.87 * mm, "tapClearance" : 10, "startFromSketch" : true, "locations" : qUnion([Q0]), "scope" : qUnion([Q1]), "majorDiameter" : 12 * mm});
        }
    });
